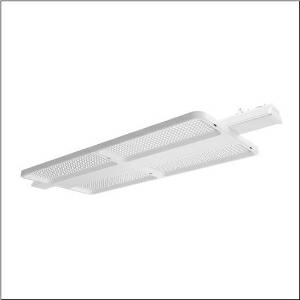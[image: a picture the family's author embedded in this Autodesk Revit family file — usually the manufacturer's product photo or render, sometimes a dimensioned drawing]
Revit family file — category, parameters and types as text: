
# Revit family: highbay_11_fur_licross_r__tragschiene_maxi_51hn11db4xla_b5ea
name_source: partatom
category: Lighting Fixtures
units: mm (PartAtom-declared; Revit-internal decimal feet)

## family parameters
Cut with Voids When Loaded = No
Host = Face
Light Source = No
Part Type = Normal
Room Calculation Point = No
Round Connector Dimension = Use Diameter
Shared = No

## types (1)
- --- (1 x LED, 70000 lm, 372.9 W, 4000K)
    Apparent Load = 373 VA
    CIE Flux Codes = 85 97 100 100 100
    Color Rendering = 80
    Color Temperature = 4000K
    Default Elevation = 1800 mm
    Description = high bay luminaire Highbay 11 for Licross® trunking rail maxi; direct symmetric narrow distribution, light control with lens of PMMA; UGR ≤ 22 (X = 4H | Y = 8H | S = 0.25H | reflection values 70/50/20); luminous flux: 70.000lm; light colour: 840, colour temperature: 4000K, MacAdam ≤ 2 SDCM (initial), colour rendering: CRI > 80; luminous efficacy: 187,7lm/W; rated service life: 50.000h (L95/B50) at AT= 25°C; control: DALI 2; luminaire connection: plug, 5-pole, with phase selectionmains connection: 230..240V, AC 50/60Hz; connected load: 372,9W; protection rating (complete): IP64; insulation class (complete): insulation class I (protective earthing); protection symbol: D; impact resistance: IK07; certification: CE, ENEC, VDE, UKCA; internal wiring halogen-free; luminaire LABS conformity tested according to VDMA 24364:2018-05; corresponds to IFS (International Featured Standards) requirements for safety and quality in the food industry; housing frame of high-performance plastic PA6, matt traffic white (RAL 9016); cover of PMMA; fixing on rail side of steel, galvanised, white; blank cover of PC/ABS, traffic white (RAL 9016); dimension (LxWxH): 1.250 x 442 x 71mm; permissible operating ambient temperature: -40..+50°C (reducing of maximum allowable ambient temperature of 5°C with ceiling mounting); packaging unit: 1 piece
    Height = 72 mm  [stored 0.23622 ft]
    Lamp = 1 x LED
    Lamp Light Flux = 70000 lm
    Lamp Power = 372.9 W
    Lamp count = 1
    Length = 946 mm
    Luminous efficacy = 188 lm/W
    Manufacturer = Siteco
    ModVariant = No
    Model = 51HN11DB4XLA
    Mounting Place = Ceiling
    Mounting Type = Pendant
    Number of Poles = 1
    OnlyDefault = Yes
    Power Factor = 1
    Product Name = Highbay 11 für Licross® Tragschiene maxi
    Product group = high bay luminaire
    ProductGroupID = 901
    Protection Class = Protection class I
    Protection Degree = IP 64
    RLX_Detail_Level = 1
    RLX_Emergency_Light_Flux = 0 lm
    RLX_Emergency_Type = 0
    RLX_Emergency_Type_DB = No
    RlxData = <blob elided: 24369 chars, md5=a686f562>
    Socket = socket
    Standby Power = 0 W
    System Light Flux = 70001 lm
    System Power = 373 W
    Type Comments = factory setting: luminous flux: 100 % | dim-lin: 254 | 837 mA
    Type Image = l_1361711.jpg
    URL = http://relux.com
    VarID = @adj_020819
    Voltage = 0 V
    Weight = 0.00 kg
    Width = 442 mm

note: [stored X ft] marks values corroborated as IEEE doubles in the binary element streams (Revit-internal decimal feet)

## geometry (parser evidence)
native form markers: Blend x4, Sweep x11
no freeform markers — native parametric forms only
